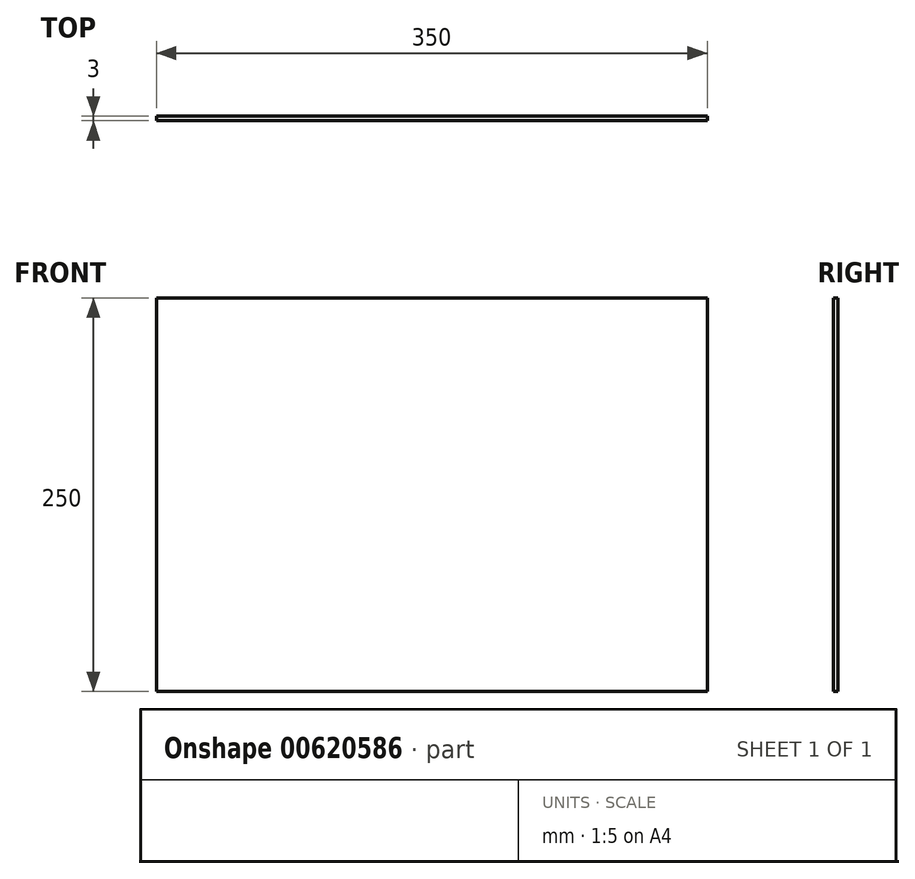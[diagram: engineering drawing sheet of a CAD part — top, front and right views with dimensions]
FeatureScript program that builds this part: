
annotation { "Feature Type Name" : "Feature", "Feature Type Description" : "" }
export const myFeature = defineFeature(function(context is Context, id is Id, definition is map)
    precondition{}
    {
        {
            var Q0;
            Q0=qCreatedBy(makeId("Front.planeOp"),FACE);
            var sketch = newSketch(context, id + "F0", { "sketchPlane" : qUnion([Q0])});
            skLineSegment(sketch, "E0.bottom", {"start": v(-175, -125) * mm, "end": v(175, -125) * mm});
            skLineSegment(sketch, "E0.top", {"start": v(-175, 125) * mm, "end": v(175, 125) * mm});
            skLineSegment(sketch, "E0.left", {"start": v(-175, -125) * mm, "end": v(-175, 125) * mm});
            skLineSegment(sketch, "E0.right", {"start": v(175, -125) * mm, "end": v(175, 125) * mm});
            skPoint(sketch, "E0.middle", {"position": v(0, 0) * mm});
            skSolve(sketch);
        }
        {
            var Q0;
            Q0=makeQuery(id+"F0.imprint","IMPRINT",FACE,{"disambiguationData":[TD([[makeQuery(id+"F0.imprint","IMPRINT",EDGE,{"derivedFrom":sQuery(id+"F0.wireOp",EDGE,"E0.bottom")}),1.0]])]});
            extrude(context, id + "F1", {"entities" : qUnion([Q0]), "depth" : 3 * mm, "offsetDistance" : 25 * mm});
        }
    });
